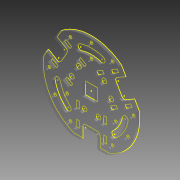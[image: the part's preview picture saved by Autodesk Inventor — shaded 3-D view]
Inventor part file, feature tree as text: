
AUTODESK INVENTOR PART (.ipt)
format: ipt  version: 2015 (Build 190159000, 159)  size: 449,024 bytes
history: native  units: mm
features: sketch x8, extrude x7, projected_geometry x4, pattern_circular x3, fillet x1
ambient origin geometry x8: Origin, YZ Plane, XZ Plane, XY Plane, X Axis, Y Axis, Z Axis, Center Point
bodies: Solid1 (feature_tree)
feature tree (23):
  extrude  "Extrusion1"  Depth=47.907mm
  sketch  "Sketch2"  dims[d2=120.0deg d3=120.0deg]
  sketch  "Sketch3"  dims[d4=47.907mm d5=47.907mm]
  extrude  "Extrusion2"  TaperAngle=120.0deg  [1 undecoded]
  extrude  "Extrusion3"  Depth=47.907mm
  extrude  "Extrusion4"  Depth=51.5mm
  extrude  "Extrusion5"  Depth=3.0mm TaperAngle=0.0deg
  pattern_circular  "Circular Pattern1"  [2 undecoded]
  extrude  "Extrusion6"  Depth=7.0mm
  extrude  "Extrusion7"  Depth=7.0mm
  pattern_circular  "Circular Pattern2"  [2 undecoded]
  fillet  "Fillet1"  Radius=7.0mm
  pattern_circular  "Circular Pattern3"  [2 undecoded]
  sketch  "Sketch9"  dims[d13=20.006mm d14=15.0mm d15=7.0mm d16=7.0mm d17=11.0mm d18=7.0mm d19=32.0mm d20=3.0mm d21=3.0mm d22=3.0mm d23=0.0mm d24=3.0mm d25=0.0mm d26=18.5mm d28=14.0mm d29=3.0mm d30=0.0mm d31=12.8mm d32=12.8mm d33=3.0mm d34=0.0mm d35=30.0mm d36=360.0deg d38=3.0mm d39=3.0mm d40=3.0mm d41=120.0deg d42=120.0deg d43=90.0mm d44=60.0mm d45=3.0mm d46=3.0mm d47=3.0mm d48=3.0mm d49=0.0mm d50=7.330383mm d51=7.330383mm d52=6.0mm d53=34.0mm d54=3.0mm d55=0.0mm d56=30.0mm d57=360.0deg d59=3.0mm d60=30.0mm d61=360.0deg d63=3.0mm d64=3.0mm d65=3.0mm d66=3.0mm d67=30.0deg d68=30.0deg d69=30.0deg d70=30.0deg d71=30.0deg d72=30.0deg d73=3.0mm d74=3.0mm]
  sketch  "Sketch1"  dims[d0=100.0mm d1=47.907mm]
  projected_geometry  "Projected Loop1"
  sketch  "Sketch4"  dims[d6=51.5mm d7=51.5mm]
  sketch  "Sketch5"  dims[d8=51.5mm d9=3.0mm d10=0.0mm]
  sketch  "Sketch6"  dims[d11=5.0mm]
  projected_geometry  "Projected Loop2"
  sketch  "Sketch7"  dims[d12=5.0mm]
  projected_geometry  "Projected Loop3"
  projected_geometry  "Projected Loop5"
note: 7 required parameter values undecoded (feature->parameter linkage not recoverable at this tier; creation-order binding heuristic only, values carry confidence <= 0.55)
